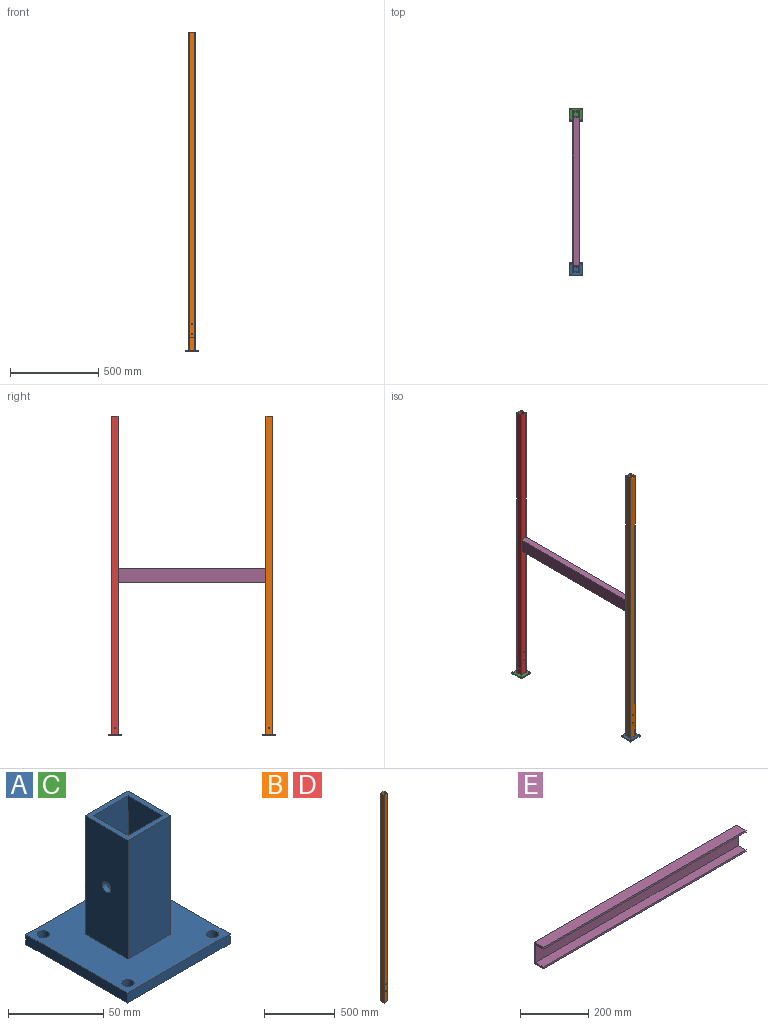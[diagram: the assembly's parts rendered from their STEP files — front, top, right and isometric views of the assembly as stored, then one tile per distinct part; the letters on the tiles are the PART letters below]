
ASSEMBLY  parts=5 mates=3
PART A: 22 faces, bbox 76.2x75.3x82.6 mm
  f0: plane 76.2x75.32mm, normal (0,0,1), area 4604.9mm2, adj f1,f2,f3,f4,f9,f10,f11,f12
  f1: plane 75.32x6.35mm, normal (1,0,0), area 478.3mm2, adj f0,f2,f4,f5
  f2: plane 76.2x6.35mm, normal (0,1,0), area 483.9mm2, adj f0,f1,f3,f5
  f3: plane 75.32x6.35mm, normal (-1,0,0), area 478.3mm2, adj f0,f2,f4,f5
  f4: plane 76.2x6.35mm, normal (0,-1,0), area 483.9mm2, adj f0,f1,f3,f5
  f5: plane 76.2x75.32mm, normal (0,0,-1), area 5613mm2, adj f1,f2,f3,f4,f18,f19,f20,f21
  f6: plane 76.2x25.4mm, normal (0,-1,0), area 1935.5mm2, adj f7,f13,f14,f15
  f7: plane 76.2x25.4mm, normal (-1,0,0), area 1903.8mm2, adj f6,f8,f14,f15,f17
  f8: plane 76.2x25.4mm, normal (0,1,0), area 1935.5mm2, adj f7,f13,f14,f15
  f9: plane 76.2x31.75mm, normal (1,0,0), area 2387.7mm2, adj f0,f10,f12,f14,f17
  f10: plane 76.2x31.75mm, normal (0,1,0), area 2419.3mm2, adj f0,f9,f11,f14
  f11: plane 76.2x31.75mm, normal (-1,0,0), area 2387.7mm2, adj f0,f10,f12,f14,f16
  f12: plane 76.2x31.75mm, normal (0,-1,0), area 2419.3mm2, adj f0,f9,f11,f14
  f13: plane 76.2x25.4mm, normal (1,0,0), area 1903.8mm2, adj f6,f8,f14,f15,f16
  f14: plane 31.75x31.75mm, normal (0,0,1), area 362.9mm2, adj f6,f7,f8,f9,f10,f11,f12,f13
  f15: plane 25.4x25.4mm, normal (0,0,1), area 645.2mm2, adj f6,f7,f8,f13
  f16: cylinder r=3.17mm len=6.35mm, axis (-1,0,0), area 63.3mm2, adj f11,f13
  f17: cylinder r=3.17mm len=6.35mm, axis (-1,0,0), area 63.3mm2, adj f7,f9
  f18: cylinder r=3.17mm len=6.35mm, axis (0,0,1), area 126.7mm2, adj f0,f5
  f19: cylinder r=3.17mm len=6.35mm, axis (0,0,1), area 126.7mm2, adj f0,f5
  f20: cylinder r=3.17mm len=6.35mm, axis (0,0,1), area 126.7mm2, adj f0,f5
  f21: cylinder r=3.17mm len=6.35mm, axis (0,0,1), area 126.7mm2, adj f0,f5
PART B: 16 faces, bbox 38.1x38.1x1803.4 mm
  f0: plane 1803.4x31.75mm, normal (0,1,0), area 57194.6mm2, adj f1,f7,f8,f9,f13,f15
  f1: plane 1803.4x31.75mm, normal (1,0,0), area 57226.3mm2, adj f0,f2,f8,f9,f11
  f2: plane 1803.4x31.75mm, normal (0,-1,0), area 57194.6mm2, adj f1,f7,f8,f9,f12,f14
  f3: plane 1803.4x38.1mm, normal (-1,0,0), area 68677.9mm2, adj f4,f6,f8,f9,f11
  f4: plane 1803.4x38.1mm, normal (0,-1,0), area 68646.2mm2, adj f3,f5,f8,f9,f13,f15
  f5: plane 1803.4x38.1mm, normal (1,0,0), area 68677.9mm2, adj f4,f6,f8,f9,f10
  f6: plane 1803.4x38.1mm, normal (0,1,0), area 68646.2mm2, adj f3,f5,f8,f9,f12,f14
  f7: plane 1803.4x31.75mm, normal (-1,0,0), area 57226.3mm2, adj f0,f2,f8,f9,f10
  f8: plane 38.1x38.1mm, normal (0,0,1), area 443.5mm2, adj f0,f1,f2,f3,f4,f5,f6,f7
  f9: plane 38.1x38.1mm, normal (0,0,-1), area 443.5mm2, adj f0,f1,f2,f3,f4,f5,f6,f7
  f10: cylinder r=3.17mm len=6.35mm, axis (-1,0,0), area 63.3mm2, adj f5,f7
  f11: cylinder r=3.17mm len=6.35mm, axis (-1,0,0), area 63.3mm2, adj f1,f3
  f12: cylinder r=3.17mm len=6.35mm, axis (0,-1,0), area 63.3mm2, adj f2,f6
  f13: cylinder r=3.17mm len=6.35mm, axis (0,-1,0), area 63.3mm2, adj f0,f4
  f14: cylinder r=3.17mm len=6.35mm, axis (0,-1,0), area 63.3mm2, adj f2,f6
  f15: cylinder r=3.17mm len=6.35mm, axis (0,-1,0), area 63.3mm2, adj f0,f4
PART C: same geometry as A
PART D: same geometry as B
PART E: 10 faces, bbox 838.2x38x76.2 mm
  f0: plane 838.2x38.05mm, normal (0,0,-1), area 31892.8mm2, adj f1,f7,f8,f9
  f1: plane 838.2x76.2mm, normal (0,1,0), area 63870.8mm2, adj f0,f2,f8,f9
  f2: plane 838.2x38.05mm, normal (0,0,1), area 31892.8mm2, adj f1,f3,f8,f9
  f3: plane 838.2x6.35mm, normal (0,-1,0), area 5322.6mm2, adj f2,f4,f8,f9
  f4: plane 838.2x31.75mm, normal (0,0,-1), area 26612.8mm2, adj f3,f5,f8,f9
  f5: plane 838.2x63.5mm, normal (0,-1,0), area 53225.7mm2, adj f4,f6,f8,f9
  f6: plane 838.2x31.75mm, normal (0,0,1), area 26612.8mm2, adj f5,f7,f8,f9
  f7: plane 838.2x6.35mm, normal (0,-1,0), area 5322.6mm2, adj f0,f6,f8,f9
  f8: plane 76.2x38.05mm, normal (1,0,0), area 883.2mm2, adj f0,f1,f2,f3,f4,f5,f6,f7
  f9: plane 76.2x38.05mm, normal (-1,0,0), area 883.2mm2, adj f0,f1,f2,f3,f4,f5,f6,f7
PLACE A t=(0,-876.3,0)mm
PLACE B t=(-19.05,-895.35,6.35)mm
PLACE C at identity fixed
PLACE D t=(-19.05,-19.05,6.35)mm
PLACE E rot(axis=(0,0,1),90deg) t=(-19.05,-857.25,869.95)mm
MATE fastened C.f0 <-> D.f9  axis (0,0,1) through (15.88,-15.88,6.35)mm
MATE fastened D.f4 <-> E.f8  axis (0,-1,0) through (-19.05,-19.05,908.05)mm
MATE parallel D.f10 <-> E.f1  axis (-1,0,0) through (-19.05,0,44.45)mm
